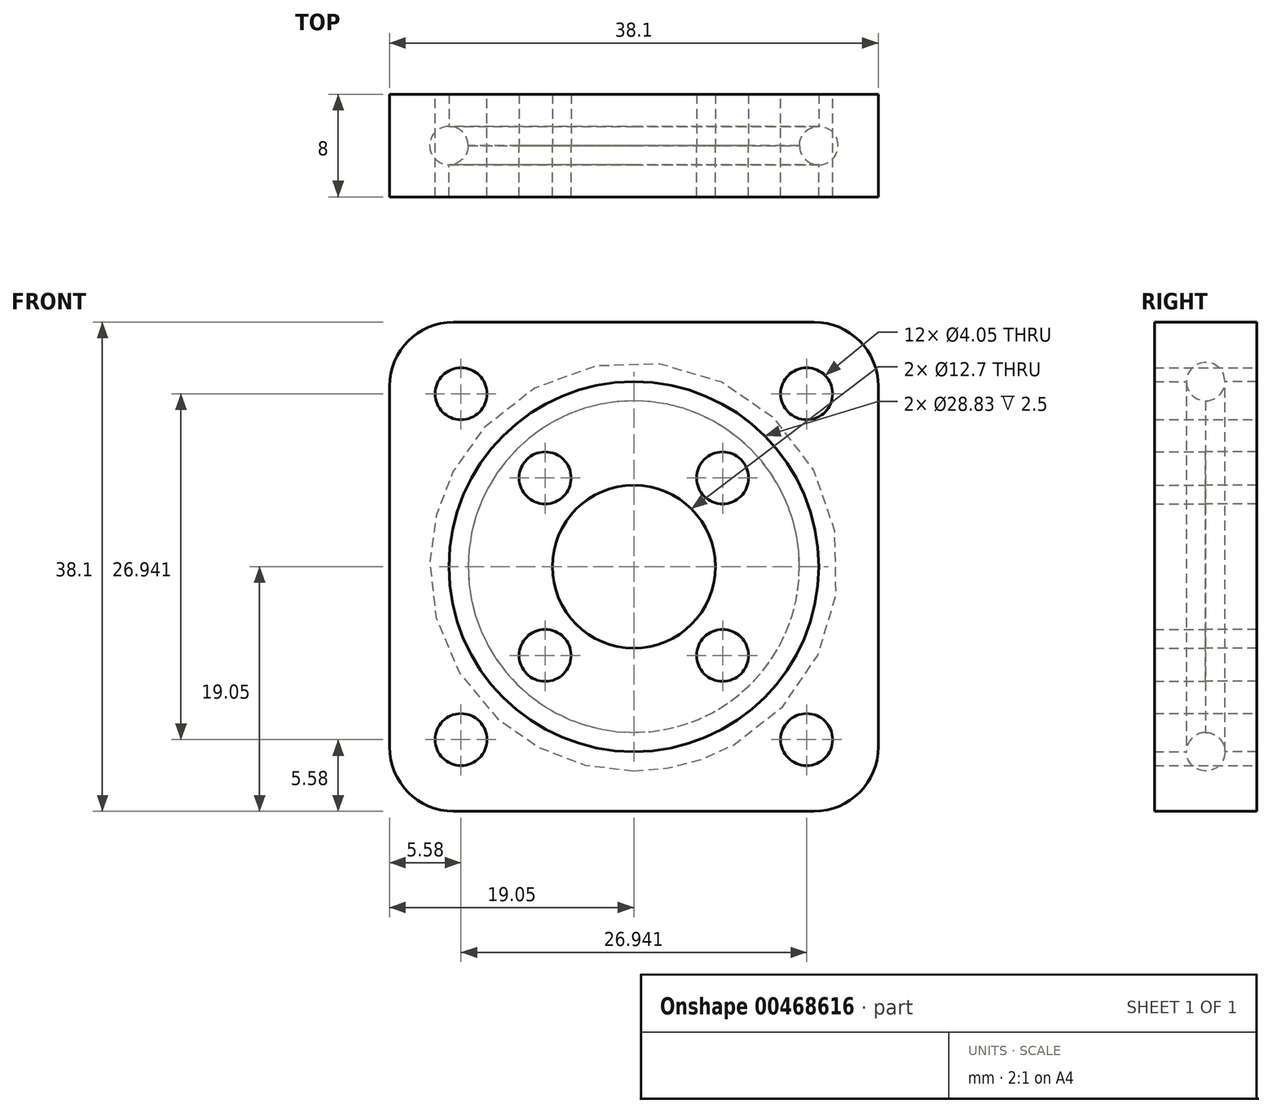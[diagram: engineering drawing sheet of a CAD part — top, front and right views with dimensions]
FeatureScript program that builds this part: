
annotation { "Feature Type Name" : "Feature", "Feature Type Description" : "" }
export const myFeature = defineFeature(function(context is Context, id is Id, definition is map)
    precondition{}
    {
        {
            var Q0;
            Q0=qCreatedBy(makeId("Front.planeOp"),FACE);
            var sketch = newSketch(context, id + "F0", { "sketchPlane" : qUnion([Q0])});
            skCircle(sketch, "E0", {"center": v(0, 0) * mm, "radius": 6.35 * mm});
            skCircle(sketch, "E1.cCircle", {"center": v(0, 0) * mm, "radius": 9.78 * mm, "construction": true});
            skLineSegment(sketch, "E1.0", {"start": v(-6.91, 6.91) * mm, "end": v(6.91, 6.91) * mm, "construction": true});
            skLineSegment(sketch, "E1.1", {"start": v(6.91, 6.91) * mm, "end": v(6.91, -6.91) * mm, "construction": true});
            skLineSegment(sketch, "E1.2", {"start": v(6.91, -6.91) * mm, "end": v(-6.91, -6.91) * mm, "construction": true});
            skLineSegment(sketch, "E1.3", {"start": v(-6.91, -6.91) * mm, "end": v(-6.91, 6.91) * mm, "construction": true});
            skCircle(sketch, "E2", {"center": v(-6.91, 6.91) * mm, "radius": 2.02 * mm});
            skLineSegment(sketch, "E3.bottom", {"start": v(19.05, 19.05) * mm, "end": v(-19.05, 19.05) * mm});
            skLineSegment(sketch, "E3.top", {"start": v(19.05, -19.05) * mm, "end": v(-19.05, -19.05) * mm});
            skLineSegment(sketch, "E3.left", {"start": v(19.05, 19.05) * mm, "end": v(19.05, -19.05) * mm});
            skLineSegment(sketch, "E3.right", {"start": v(-19.05, 19.05) * mm, "end": v(-19.05, -19.05) * mm});
            skCircle(sketch, "E4.cCircle", {"center": v(0, 0) * mm, "radius": 19.05 * mm, "construction": true});
            skLineSegment(sketch, "E4.0", {"start": v(-13.47, 13.47) * mm, "end": v(13.47, 13.47) * mm, "construction": true});
            skLineSegment(sketch, "E4.1", {"start": v(13.47, 13.47) * mm, "end": v(13.47, -13.47) * mm, "construction": true});
            skLineSegment(sketch, "E4.2", {"start": v(13.47, -13.47) * mm, "end": v(-13.47, -13.47) * mm, "construction": true});
            skLineSegment(sketch, "E4.3", {"start": v(-13.47, -13.47) * mm, "end": v(-13.47, 13.47) * mm, "construction": true});
            skCircle(sketch, "E5", {"center": v(-13.47, 13.47) * mm, "radius": 2.02 * mm});
            skCircle(sketch, "E6.1.0", {"center": v(-6.91, -6.91) * mm, "radius": 2.02 * mm});
            skCircle(sketch, "E6.1.1", {"center": v(-13.47, -13.47) * mm, "radius": 2.02 * mm});
            skCircle(sketch, "E6.2.0", {"center": v(6.91, -6.91) * mm, "radius": 2.02 * mm});
            skCircle(sketch, "E6.2.1", {"center": v(13.47, -13.47) * mm, "radius": 2.02 * mm});
            skCircle(sketch, "E7.2.3.0", {"center": v(13.47, 13.47) * mm, "radius": 2.02 * mm});
            skCircle(sketch, "E7.3.3.0", {"center": v(6.91, 6.91) * mm, "radius": 2.02 * mm});
            skCircle(sketch, "E8", {"center": v(0, 0) * mm, "radius": 14.41 * mm});
            skLineSegment(sketch, "E9", {"start": v(-6.91, 6.91) * mm, "end": v(-8.35, 8.35) * mm, "construction": true});
            skLineSegment(sketch, "E10", {"start": v(-8.35, 8.35) * mm, "end": v(-9.13, 9.13) * mm, "construction": true});
            skLineSegment(sketch, "E11", {"start": v(-9.13, 9.13) * mm, "end": v(-11.25, 11.25) * mm, "construction": true});
            skLineSegment(sketch, "E12", {"start": v(-11.25, 11.25) * mm, "end": v(-12.04, 12.04) * mm, "construction": true});
            skLineSegment(sketch, "E13", {"start": v(-12.04, 12.04) * mm, "end": v(-13.47, 13.47) * mm, "construction": true});
            skPoint(sketch, "E14", {"position": v(-10.2, 10.2) * mm});
            skSolve(sketch);
        }
        {
            var Q0;
            Q0=makeQuery(id+"F0.imprint","IMPRINT",FACE,{"disambiguationData":[TD([[makeQuery(id+"F0.imprint","IMPRINT",EDGE,{"derivedFrom":sQuery(id+"F0.wireOp",EDGE,"E3.bottom")}),1.0]])]});
            extrude(context, id + "F1", {"entities" : qUnion([Q0]), "depth" : 8 * mm, "offsetDistance" : 25 * mm, "symmetric" : true});
        }
        {
            var Q0;
            Q0=makeQuery(id+"F0.imprint","IMPRINT",FACE,{"disambiguationData":[TD([[makeQuery(id+"F0.imprint","IMPRINT",EDGE,{"derivedFrom":sQuery(id+"F0.wireOp",EDGE,"E0")}),-1.0]])]});
            extrude(context, id + "F2", {"entities" : qUnion([Q0]), "depth" : 4 * mm, "offsetDistance" : 25 * mm});
        }
        {
            var Q0;
            Q0=makeQuery(id+"F0.imprint","IMPRINT",FACE,{"disambiguationData":[TD([[makeQuery(id+"F0.imprint","IMPRINT",EDGE,{"derivedFrom":sQuery(id+"F0.wireOp",EDGE,"E0")}),-1.0]])]});
            extrude(context, id + "F3", {"entities" : qUnion([Q0]), "oppositeDirection" : true, "depth" : 4 * mm, "offsetDistance" : 25 * mm});
        }
        {
            var Q0;
            Q0=makeQuery(id+"F1.opExtrude","SWEPT_EDGE",EDGE,{"disambiguationData":[OSD([sQuery(id+"F0.wireOp",EDGE,"E3.bottom"),sQuery(id+"F0.wireOp",EDGE,"E3.right")])]});
            var Q1;
            Q1=makeQuery(id+"F1.opExtrude","SWEPT_EDGE",EDGE,{"disambiguationData":[OSD([sQuery(id+"F0.wireOp",EDGE,"E3.bottom"),sQuery(id+"F0.wireOp",EDGE,"E3.left")])]});
            var Q2;
            Q2=makeQuery(id+"F1.opExtrude","SWEPT_EDGE",EDGE,{"disambiguationData":[OSD([sQuery(id+"F0.wireOp",EDGE,"E3.top"),sQuery(id+"F0.wireOp",EDGE,"E3.left")])]});
            var Q3;
            Q3=makeQuery(id+"F1.opExtrude","SWEPT_EDGE",EDGE,{"disambiguationData":[OSD([sQuery(id+"F0.wireOp",EDGE,"E3.top"),sQuery(id+"F0.wireOp",EDGE,"E3.right")])]});
            fillet(context, id + "F4", {"entities" : qUnion([Q0, Q1, Q2, Q3]), "radius" : 5 * mm, "tangentPropagation" : true, "allowEdgeOverflow" : false});
        }
        {
            var Q0;
            Q0=qCreatedBy(makeId("Right.planeOp"),FACE);
            var sketch = newSketch(context, id + "F5", { "sketchPlane" : qUnion([Q0])});
            skLineSegment(sketch, "E15.0", {"start": v(0, -14.41) * mm, "end": v(0, 14.41) * mm});
            skCircle(sketch, "E16", {"center": v(0, 14.41) * mm, "radius": 1.5 * mm});
            skSolve(sketch);
        }
        {
            var Q0;
            Q0=makeQuery(id+"F5.imprint","IMPRINT",FACE,{"disambiguationData":[TD([[makeQuery(id+"F5.imprint","IMPRINT",EDGE,{"derivedFrom":sQuery(id+"F5.wireOp",EDGE,"E16")}),1.0]])]});
            var Q1;
            Q1=sQuery(id+"F0.wireOp",EDGE,"E8");
            sweep(context, id + "F6", {"operationType" : NewBodyOperationType.REMOVE, "profiles" : qUnion([Q0]), "path" : qUnion([Q1])});
        }
    });
